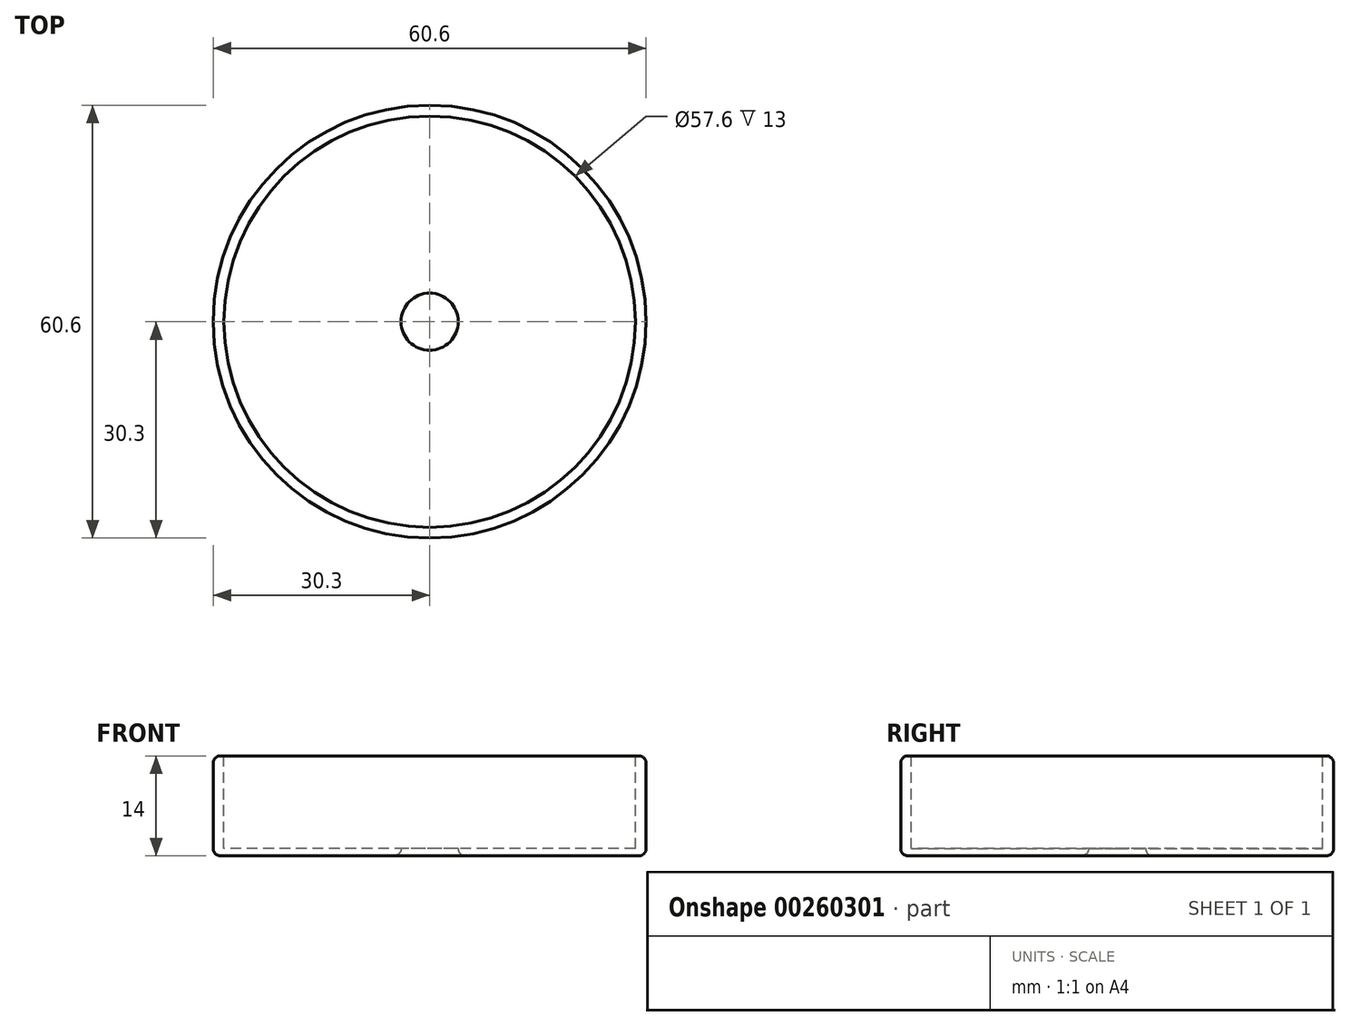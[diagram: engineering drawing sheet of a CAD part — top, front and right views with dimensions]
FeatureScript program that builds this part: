
annotation { "Feature Type Name" : "Feature", "Feature Type Description" : "" }
export const myFeature = defineFeature(function(context is Context, id is Id, definition is map)
    precondition{}
    {
        {
            var Q0;
            Q0=qCreatedBy(makeId("Top.planeOp"),FACE);
            var sketch = newSketch(context, id + "F0", { "sketchPlane" : qUnion([Q0])});
            skCircle(sketch, "E0", {"center": v(0, 0) * mm, "radius": 30.3 * mm});
            skSolve(sketch);
        }
        {
            var Q0;
            Q0 = qSketchRegion(id + "F0", true);
            extrude(context, id + "F1", {"entities" : qUnion([Q0]), "depth" : 14 * mm});
        }
        {
            var Q0;
            Q0=makeQuery(id+"F1.opExtrude","CAP_FACE",FACE,{"disambiguationData":[OSD([sQuery(id+"F0.wireOp",EDGE,"E0")])],"isStart":false});
            var sketch = newSketch(context, id + "F2", { "sketchPlane" : qUnion([Q0])});
            skCircle(sketch, "E1", {"center": v(0, 0) * mm, "radius": 28.8 * mm});
            skSolve(sketch);
        }
        {
            var Q0;
            Q0 = qSketchRegion(id + "F2", true);
            extrude(context, id + "F3", {"entities" : qUnion([Q0]), "operationType" : NewBodyOperationType.REMOVE, "oppositeDirection" : true, "depth" : 13 * mm});
        }
        {
            var Q0;
            Q0=makeQuery(id+"F3.boolean.opBoolean","COPY",FACE,{"derivedFrom":makeQuery(id+"F3.opExtrude","CAP_FACE",FACE,{"disambiguationData":[OSD([sQuery(id+"F2.wireOp",EDGE,"E1")])],"isStart":false})});
            var sketch = newSketch(context, id + "F4", { "sketchPlane" : qUnion([Q0])});
            skCircle(sketch, "E2", {"center": v(0, 0) * mm, "radius": 4 * mm});
            skSolve(sketch);
        }
        {
            var Q0;
            Q0 = qSketchRegion(id + "F4", true);
            extrude(context, id + "F5", {"entities" : qUnion([Q0]), "operationType" : NewBodyOperationType.REMOVE, "oppositeDirection" : true, "depth" : 25.4 * mm});
        }
        {
            var Q0;
            Q0=makeQuery(id+"F1.opExtrude","CAP_FACE",FACE,{"disambiguationData":[OSD([sQuery(id+"F0.wireOp",EDGE,"E0")])],"isStart":true});
            var Q1;
            Q1=makeQuery(id+"F1.opExtrude","CAP_EDGE",EDGE,{"disambiguationData":[OSD([sQuery(id+"F0.wireOp",EDGE,"E0")])],"isStart":false});
            fillet(context, id + "F6", {"entities" : qUnion([Q0, Q1]), "radius" : 1 * mm, "tangentPropagation" : true, "allowEdgeOverflow" : false});
        }
    });
